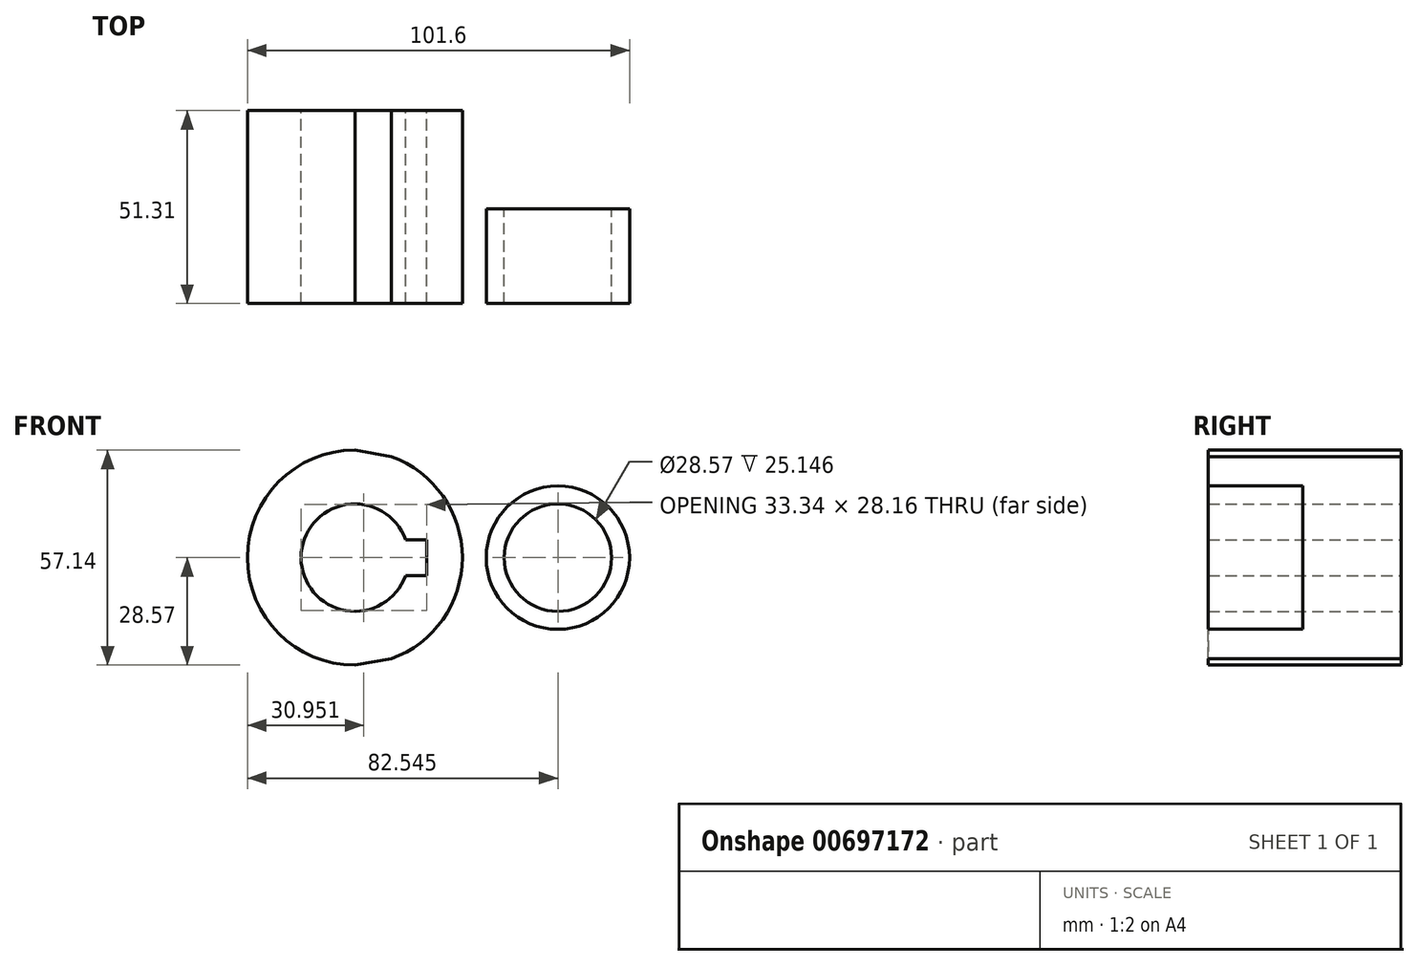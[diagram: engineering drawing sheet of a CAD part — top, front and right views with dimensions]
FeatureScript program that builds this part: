
annotation { "Feature Type Name" : "Feature", "Feature Type Description" : "" }
export const myFeature = defineFeature(function(context is Context, id is Id, definition is map)
    precondition{}
    {
        {
            var Q0;
            Q0=qCreatedBy(makeId("Front.planeOp"),FACE);
            var sketch = newSketch(context, id + "F0", { "sketchPlane" : qUnion([Q0])});
            skCircle(sketch, "E0", {"center": v(0, 0) * mm, "radius": 28.57 * mm});
            skCircle(sketch, "E1", {"center": v(53.98, 0) * mm, "radius": 19.05 * mm});
            skLineSegment(sketch, "E2", {"start": v(0, 28.58) * mm, "end": v(54.41, 19.04) * mm});
            skLineSegment(sketch, "E3", {"start": v(0, -28.58) * mm, "end": v(54.62, -19.04) * mm});
            skCircle(sketch, "E4", {"center": v(0, 0) * mm, "radius": 14.29 * mm});
            skCircle(sketch, "E5", {"center": v(53.98, 0) * mm, "radius": 14.29 * mm});
            skLineSegment(sketch, "E6.bottom", {"start": v(-19.05, 4.76) * mm, "end": v(19.05, 4.76) * mm});
            skLineSegment(sketch, "E6.top", {"start": v(-19.05, -4.76) * mm, "end": v(19.05, -4.76) * mm});
            skLineSegment(sketch, "E6.left", {"start": v(-19.05, 4.76) * mm, "end": v(-19.05, -4.76) * mm});
            skLineSegment(sketch, "E6.right", {"start": v(19.05, 4.76) * mm, "end": v(19.05, -4.76) * mm});
            skSolve(sketch);
        }
        {
            var Q0;
            {var subQ4=sQuery(id+"F0.wireOp",EDGE,"E6.left");Q0=makeQuery(id+"F0.imprint","IMPRINT",FACE,{"disambiguationData":[TD([[makeQuery(id+"F0.imprint","IMPRINT",EDGE,{"derivedFrom":subQ4}),-1.0]])]});}
            var Q1;
            {var subQ5=sQuery(id+"F0.wireOp",EDGE,"E6.left");Q1=makeQuery(id+"F0.imprint","IMPRINT",FACE,{"disambiguationData":[TD([[makeQuery(id+"F0.imprint","IMPRINT",EDGE,{"derivedFrom":subQ5}),1.0]])]});}
            var Q2;
            {var subQ0=sQuery(id+"F0.wireOp",EDGE,"E2");var subQ1=sQuery(id+"F0.wireOp",EDGE,"E0");var subQ2=makeQuery(id+"F0.imprint","INTERSECT",VERTEX,{"disambiguationData":[OD(1.0)],"derivedFrom":[subQ1,subQ0]});Q2=makeQuery(id+"F0.imprint","IMPRINT",FACE,{"disambiguationData":[TD([[makeQuery(id+"F0.imprint","IMPRINT",EDGE,{"disambiguationData":[TD([[subQ2,1.0]])],"derivedFrom":subQ1}),-1.0]])]});}
            var Q3;
            Q3=makeQuery(id+"F0.imprint","IMPRINT",FACE,{"disambiguationData":[TD([[makeQuery(id+"F0.imprint","IMPRINT",EDGE,{"derivedFrom":sQuery(id+"F0.wireOp",EDGE,"E5")}),-1.0]])]});
            extrude(context, id + "F1", {"entities" : qUnion([Q0, Q1, Q2, Q3]), "depth" : 25.15 * mm, "offsetDistance" : 25.4 * mm});
        }
        {
            var Q0;
            {var subQ4=sQuery(id+"F0.wireOp",EDGE,"E6.left");Q0=makeQuery(id+"F0.imprint","IMPRINT",FACE,{"disambiguationData":[TD([[makeQuery(id+"F0.imprint","IMPRINT",EDGE,{"derivedFrom":subQ4}),-1.0]])]});}
            var Q1;
            {var subQ5=sQuery(id+"F0.wireOp",EDGE,"E6.left");Q1=makeQuery(id+"F0.imprint","IMPRINT",FACE,{"disambiguationData":[TD([[makeQuery(id+"F0.imprint","IMPRINT",EDGE,{"derivedFrom":subQ5}),1.0]])]});}
            extrude(context, id + "F2", {"entities" : qUnion([Q0, Q1]), "operationType" : NewBodyOperationType.ADD, "oppositeDirection" : true, "depth" : 26.16 * mm, "offsetDistance" : 25.4 * mm});
        }
    });
